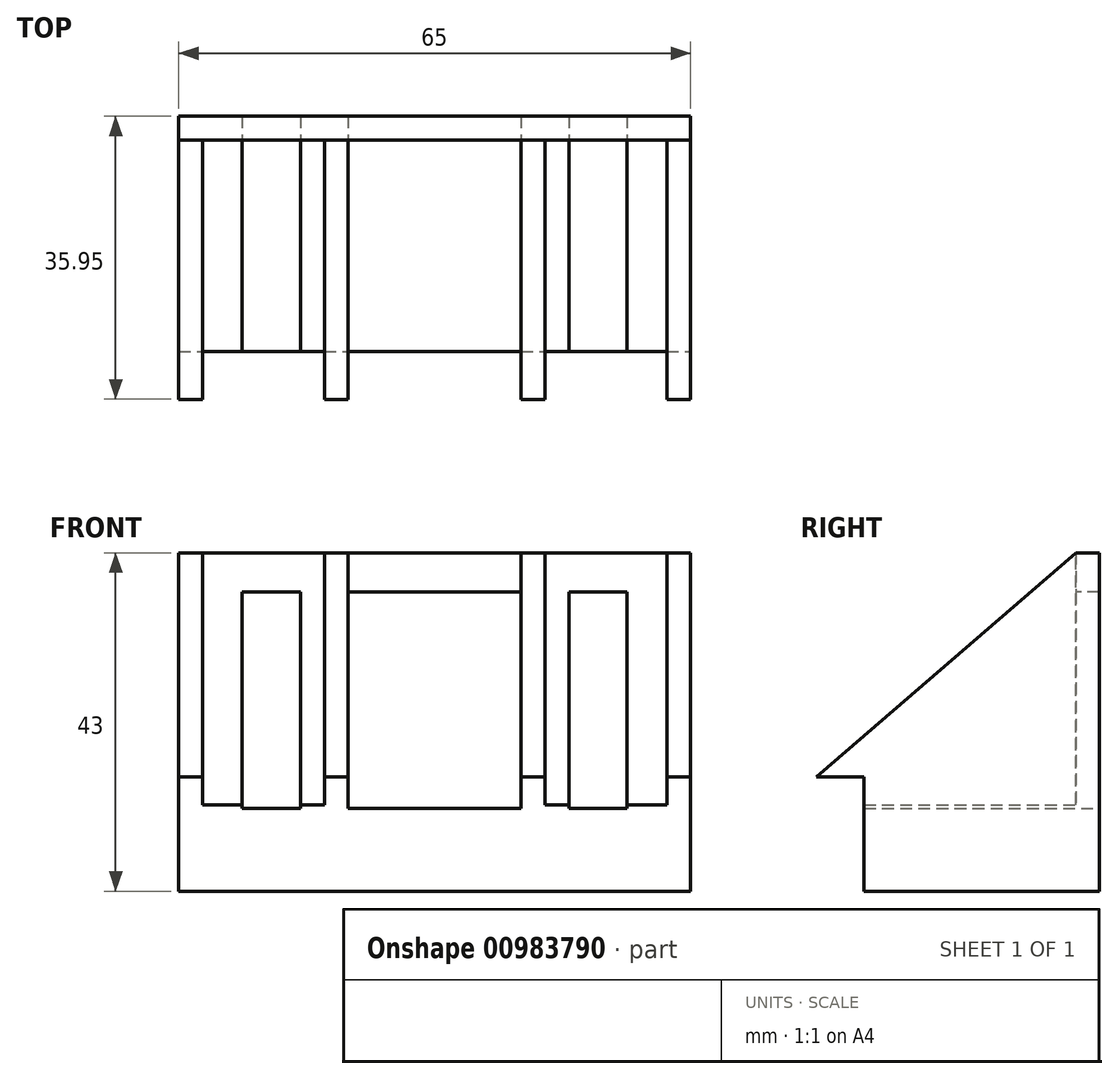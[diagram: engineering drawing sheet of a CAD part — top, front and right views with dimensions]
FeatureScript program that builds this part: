
annotation { "Feature Type Name" : "Feature", "Feature Type Description" : "" }
export const myFeature = defineFeature(function(context is Context, id is Id, definition is map)
    precondition{}
    {
        {
            var Q0;
            Q0=qCreatedBy(makeId("Front.planeOp"),FACE);
            var sketch = newSketch(context, id + "F0", { "sketchPlane" : qUnion([Q0])});
            skLineSegment(sketch, "E0.bottom", {"start": v(-32.5, 17.5) * mm, "end": v(32.5, 17.5) * mm});
            skLineSegment(sketch, "E0.top", {"start": v(-32.5, -17.5) * mm, "end": v(32.5, -17.5) * mm});
            skLineSegment(sketch, "E0.left", {"start": v(-32.5, 17.5) * mm, "end": v(-32.5, -17.5) * mm});
            skLineSegment(sketch, "E0.right", {"start": v(32.5, 17.5) * mm, "end": v(32.5, -17.5) * mm});
            skPoint(sketch, "E0.middle", {"position": v(0, 0) * mm});
            skLineSegment(sketch, "E1.bottom", {"start": v(-20.75, 15) * mm, "end": v(20.75, 15) * mm, "construction": true});
            skLineSegment(sketch, "E1.top", {"start": v(-20.75, -15) * mm, "end": v(20.75, -15) * mm, "construction": true});
            skLineSegment(sketch, "E1.left", {"start": v(-20.75, 15) * mm, "end": v(-20.75, -15) * mm, "construction": true});
            skLineSegment(sketch, "E1.right", {"start": v(20.75, 15) * mm, "end": v(20.75, -15) * mm, "construction": true});
            skLineSegment(sketch, "E2.bottom", {"start": v(-20.75, 15) * mm, "end": v(-24.45, 15) * mm});
            skLineSegment(sketch, "E2.top", {"start": v(-20.75, -15) * mm, "end": v(-24.45, -15) * mm});
            skLineSegment(sketch, "E2.left", {"start": v(-20.75, 15) * mm, "end": v(-20.75, -15) * mm});
            skLineSegment(sketch, "E2.right", {"start": v(-24.45, 15) * mm, "end": v(-24.45, -15) * mm});
            skLineSegment(sketch, "E3.MirrorCS", {"start": v(-17.05, 15) * mm, "end": v(-17.05, -15) * mm});
            skLineSegment(sketch, "E4.MirrorCS", {"start": v(-20.75, 15) * mm, "end": v(-17.05, 15) * mm});
            skLineSegment(sketch, "E5.MirrorCS", {"start": v(-20.75, -15) * mm, "end": v(-17.05, -15) * mm});
            skLineSegment(sketch, "E6.MirrorCS", {"start": v(17.05, 15) * mm, "end": v(17.05, -15) * mm});
            skLineSegment(sketch, "E7.MirrorCS", {"start": v(24.45, 15) * mm, "end": v(24.45, -15) * mm});
            skLineSegment(sketch, "E8.MirrorCS", {"start": v(20.75, -15) * mm, "end": v(24.45, -15) * mm});
            skLineSegment(sketch, "E9.MirrorCS", {"start": v(20.75, -15) * mm, "end": v(-20.75, -15) * mm, "construction": true});
            skLineSegment(sketch, "E10.MirrorCS", {"start": v(20.75, 15) * mm, "end": v(24.45, 15) * mm});
            skLineSegment(sketch, "E11.MirrorCS", {"start": v(20.75, 15) * mm, "end": v(-20.75, 15) * mm, "construction": true});
            skLineSegment(sketch, "E12.bottom", {"start": v(17.05, 15) * mm, "end": v(24.45, 15) * mm});
            skLineSegment(sketch, "E12.top", {"start": v(17.05, -15) * mm, "end": v(24.45, -15) * mm});
            skLineSegment(sketch, "E13.bottom", {"start": v(-11, 15) * mm, "end": v(11, 15) * mm});
            skLineSegment(sketch, "E13.top", {"start": v(-11, -15) * mm, "end": v(11, -15) * mm});
            skLineSegment(sketch, "E13.left", {"start": v(-11, 15) * mm, "end": v(-11, -15) * mm});
            skLineSegment(sketch, "E13.right", {"start": v(11, 15) * mm, "end": v(11, -15) * mm});
            skLineSegment(sketch, "E14.top", {"start": v(-32.5, -14.5) * mm, "end": v(32.5, -14.5) * mm});
            skLineSegment(sketch, "E14.left", {"start": v(-32.5, -17.5) * mm, "end": v(-32.5, -14.5) * mm});
            skLineSegment(sketch, "E14.right", {"start": v(32.5, -17.5) * mm, "end": v(32.5, -14.5) * mm});
            skSolve(sketch);
        }
        {
            var Q0;
            {var subQ15=sQuery(id+"F0.wireOp",EDGE,"E0.bottom");Q0=makeQuery(id+"F0.imprint","IMPRINT",FACE,{"disambiguationData":[TD([[makeQuery(id+"F0.imprint","IMPRINT",EDGE,{"derivedFrom":subQ15}),-1.0]])]});}
            extrude(context, id + "F1", {"entities" : qUnion([Q0]), "depth" : 3 * mm, "offsetDistance" : 25 * mm});
        }
        {
            var Q0;
            {var subQ15=sQuery(id+"F0.wireOp",EDGE,"E0.top");Q0=makeQuery(id+"F0.imprint","IMPRINT",FACE,{"disambiguationData":[TD([[makeQuery(id+"F0.imprint","IMPRINT",EDGE,{"derivedFrom":subQ15}),1.0]])]});}
            extrude(context, id + "F2", {"entities" : qUnion([Q0]), "operationType" : NewBodyOperationType.ADD, "depth" : 40 * mm, "offsetDistance" : 25 * mm});
        }
        {
            var Q0;
            {var subQ0=sQuery(id+"F0.wireOp",EDGE,"E0.left");Q0=makeQuery(id+"F2.boolean.opBoolean","MERGE",FACE,{"derivedFrom":[makeQuery(id+"F1.opExtrude","SWEPT_FACE",FACE,{"disambiguationData":[OSD([subQ0])]}),makeQuery(id+"F2.opExtrude","SWEPT_FACE",FACE,{"disambiguationData":[OSD([subQ0])]})]});}
            var sketch = newSketch(context, id + "F3", { "sketchPlane" : qUnion([Q0])});
            skLineSegment(sketch, "E15", {"start": v(3, 17.5) * mm, "end": v(40, -14.5) * mm});
            skLineSegment(sketch, "E16", {"start": v(40, -14.5) * mm, "end": v(3, -14.5) * mm});
            skLineSegment(sketch, "E17", {"start": v(3, -14.5) * mm, "end": v(3, 17.5) * mm});
            skLineSegment(sketch, "E18", {"start": v(3, 17.5) * mm, "end": v(45.34, 20.76) * mm});
            skLineSegment(sketch, "E19", {"start": v(45.34, 20.76) * mm, "end": v(40, -14.5) * mm});
            skSolve(sketch);
        }
        {
            var Q0;
            Q0=makeQuery(id+"F1.opExtrude","CAP_FACE",FACE,{"disambiguationData":[OSD([sQuery(id+"F0.wireOp",EDGE,"E0.bottom"),sQuery(id+"F0.wireOp",EDGE,"E0.left"),sQuery(id+"F0.wireOp",EDGE,"E0.right"),sQuery(id+"F0.wireOp",EDGE,"E2.bottom"),sQuery(id+"F0.wireOp",EDGE,"E2.right"),sQuery(id+"F0.wireOp",EDGE,"E3.MirrorCS"),sQuery(id+"F0.wireOp",EDGE,"E4.MirrorCS"),sQuery(id+"F0.wireOp",EDGE,"E6.MirrorCS"),sQuery(id+"F0.wireOp",EDGE,"E7.MirrorCS"),sQuery(id+"F0.wireOp",EDGE,"E10.MirrorCS"),sQuery(id+"F0.wireOp",EDGE,"E12.bottom"),sQuery(id+"F0.wireOp",EDGE,"E13.bottom"),sQuery(id+"F0.wireOp",EDGE,"E13.left"),sQuery(id+"F0.wireOp",EDGE,"E13.right"),sQuery(id+"F0.wireOp",EDGE,"E14.top")])],"isStart":false});
            var sketch = newSketch(context, id + "F4", { "sketchPlane" : qUnion([Q0])});
            skLineSegment(sketch, "E20.bottom", {"start": v(-11, -14.5) * mm, "end": v(-14, -14.5) * mm});
            skLineSegment(sketch, "E20.top", {"start": v(-11, 17.5) * mm, "end": v(-14, 17.5) * mm});
            skLineSegment(sketch, "E20.left", {"start": v(-11, -14.5) * mm, "end": v(-11, 17.5) * mm});
            skLineSegment(sketch, "E20.right", {"start": v(-14, -14.5) * mm, "end": v(-14, 17.5) * mm});
            skLineSegment(sketch, "E21.MirrorCS", {"start": v(11, -14.5) * mm, "end": v(11, 17.5) * mm});
            skLineSegment(sketch, "E22.MirrorCS", {"start": v(14, -14.5) * mm, "end": v(14, 17.5) * mm});
            skLineSegment(sketch, "E23.MirrorCS", {"start": v(11, -14.5) * mm, "end": v(14, -14.5) * mm});
            skLineSegment(sketch, "E24.MirrorCS", {"start": v(11, 17.5) * mm, "end": v(14, 17.5) * mm});
            skSolve(sketch);
        }
        {
            var Q0;
            {var subQ3=sQuery(id+"F4.wireOp",EDGE,"E20.bottom");Q0=makeQuery(id+"F4.imprint","IMPRINT",FACE,{"disambiguationData":[TD([[makeQuery(id+"F4.imprint","IMPRINT",EDGE,{"derivedFrom":subQ3}),1.0]])]});}
            var Q1;
            Q1=makeQuery(id+"F4.imprint","IMPRINT",FACE,{"disambiguationData":[TD([[makeQuery(id+"F4.imprint","IMPRINT",EDGE,{"derivedFrom":sQuery(id+"F4.wireOp",EDGE,"E22.MirrorCS")}),1.0]])]});
            extrude(context, id + "F5", {"entities" : qUnion([Q0, Q1]), "operationType" : NewBodyOperationType.ADD, "depth" : 37 * mm, "offsetDistance" : 25 * mm});
        }
        {
            var Q0;
            {var subQ0=sQuery(id+"F0.wireOp",EDGE,"E0.right");Q0=makeQuery(id+"F2.boolean.opBoolean","MERGE",FACE,{"derivedFrom":[makeQuery(id+"F1.opExtrude","SWEPT_FACE",FACE,{"disambiguationData":[OSD([subQ0])]}),makeQuery(id+"F2.opExtrude","SWEPT_FACE",FACE,{"disambiguationData":[OSD([subQ0])]})]});}
            var sketch = newSketch(context, id + "F6", { "sketchPlane" : qUnion([Q0])});
            skLineSegment(sketch, "E25", {"start": v(-3, 17.5) * mm, "end": v(-40, -14.5) * mm});
            skLineSegment(sketch, "E26", {"start": v(-40, -14.5) * mm, "end": v(-3, -14.5) * mm});
            skLineSegment(sketch, "E27", {"start": v(-3, -14.5) * mm, "end": v(-3, 17.5) * mm});
            skSolve(sketch);
        }
        {
            var Q0;
            Q0=makeQuery(id+"F6.imprint","IMPRINT",FACE,{"disambiguationData":[TD([[makeQuery(id+"F6.imprint","IMPRINT",EDGE,{"derivedFrom":sQuery(id+"F6.wireOp",EDGE,"E25")}),1.0]])]});
            extrude(context, id + "F7", {"entities" : qUnion([Q0]), "operationType" : NewBodyOperationType.ADD, "depth" : -3 * mm, "offsetDistance" : 25 * mm});
        }
        {
            var Q0;
            Q0=makeQuery(id+"F3.imprint","IMPRINT",FACE,{"disambiguationData":[TD([[makeQuery(id+"F3.imprint","IMPRINT",EDGE,{"derivedFrom":sQuery(id+"F3.wireOp",EDGE,"E15")}),-1.0]])]});
            extrude(context, id + "F8", {"entities" : qUnion([Q0]), "operationType" : NewBodyOperationType.ADD, "depth" : -3 * mm, "offsetDistance" : 25 * mm});
        }
        {
            var Q0;
            Q0=makeQuery(id+"F3.imprint","IMPRINT",FACE,{"disambiguationData":[TD([[makeQuery(id+"F3.imprint","IMPRINT",EDGE,{"derivedFrom":sQuery(id+"F3.wireOp",EDGE,"E15")}),1.0]])]});
            extrude(context, id + "F9", {"entities" : qUnion([Q0]), "operationType" : NewBodyOperationType.REMOVE, "oppositeDirection" : true, "depth" : 90 * mm, "offsetDistance" : 25 * mm});
        }
        {
            var Q0;
            Q0=makeQuery(id+"F2.opExtrude","SWEPT_FACE",FACE,{"disambiguationData":[OSD([sQuery(id+"F0.wireOp",EDGE,"E0.top")])]});
            extrude(context, id + "F10", {"entities" : qUnion([Q0]), "operationType" : NewBodyOperationType.ADD, "depth" : 8 * mm, "offsetDistance" : 25 * mm});
        }
        {
            var Q0;
            Q0=makeQuery(id+"F10.opExtrude","CAP_FACE",FACE,{"disambiguationData":[OSD([sQuery(id+"F0.wireOp",EDGE,"E0.top")])],"isStart":false});
            var sketch = newSketch(context, id + "F11", { "sketchPlane" : qUnion([Q0])});
            skLineSegment(sketch, "E28", {"start": v(-29.5, -16.45) * mm, "end": v(-14, -16.45) * mm, "construction": true});
            skCircle(sketch, "E29", {"center": v(-21.75, -16.45) * mm, "radius": 4 * mm});
            skCircle(sketch, "E30", {"center": v(-21.75, -16.45) * mm, "radius": 1.4 * mm});
            skCircle(sketch, "E31.MirrorC", {"center": v(21.75, -16.45) * mm, "radius": 4 * mm});
            skCircle(sketch, "E32.MirrorC", {"center": v(21.75, -16.45) * mm, "radius": 1.4 * mm});
            skSolve(sketch);
        }
        {
            var Q0;
            Q0=makeQuery(id+"F11.imprint","IMPRINT",FACE,{"disambiguationData":[TD([[makeQuery(id+"F11.imprint","IMPRINT",EDGE,{"derivedFrom":sQuery(id+"F11.wireOp",EDGE,"E29")}),1.0]])]});
            var Q1;
            Q1=makeQuery(id+"F11.imprint","IMPRINT",FACE,{"disambiguationData":[TD([[makeQuery(id+"F11.imprint","IMPRINT",EDGE,{"derivedFrom":sQuery(id+"F11.wireOp",EDGE,"E31.MirrorC")}),-1.0]])]});
            extrude(context, id + "F12", {"entities" : qUnion([Q0, Q1]), "operationType" : NewBodyOperationType.REMOVE, "oppositeDirection" : true, "depth" : 15 * mm, "offsetDistance" : 25 * mm});
        }
        {
            var Q0;
            Q0=makeQuery(id+"F11.imprint","IMPRINT",FACE,{"disambiguationData":[TD([[makeQuery(id+"F11.imprint","IMPRINT",EDGE,{"derivedFrom":sQuery(id+"F11.wireOp",EDGE,"E30")}),1.0]])]});
            var Q1;
            Q1=makeQuery(id+"F11.imprint","IMPRINT",FACE,{"disambiguationData":[TD([[makeQuery(id+"F11.imprint","IMPRINT",EDGE,{"derivedFrom":sQuery(id+"F11.wireOp",EDGE,"E32.MirrorC")}),-1.0]])]});
            extrude(context, id + "F13", {"entities" : qUnion([Q0, Q1]), "operationType" : NewBodyOperationType.REMOVE, "oppositeDirection" : true, "depth" : 18 * mm, "offsetDistance" : 25 * mm});
        }
        {
            var Q0;
            {var subQ0=sQuery(id+"F0.wireOp",EDGE,"E0.right");Q0=makeQuery(id+"F10.boolean.opBoolean","MERGE",FACE,{"derivedFrom":[makeQuery(id+"F7.boolean.opBoolean","MERGE",FACE,{"derivedFrom":[makeQuery(id+"F2.boolean.opBoolean","MERGE",FACE,{"derivedFrom":[makeQuery(id+"F1.opExtrude","SWEPT_FACE",FACE,{"disambiguationData":[OSD([subQ0])]}),makeQuery(id+"F2.opExtrude","SWEPT_FACE",FACE,{"disambiguationData":[OSD([subQ0])]})]}),makeQuery(id+"F7.opExtrude","CAP_FACE",FACE,{"disambiguationData":[OSD([sQuery(id+"F6.wireOp",EDGE,"E25"),sQuery(id+"F6.wireOp",EDGE,"E26"),sQuery(id+"F6.wireOp",EDGE,"E27")])],"isStart":true})]}),makeQuery(id+"F10.opExtrude","SWEPT_FACE",FACE,{"disambiguationData":[OSD([sQuery(id+"F0.wireOp",EDGE,"E0.top"),subQ0])]})]});}
            var sketch = newSketch(context, id + "F14", { "sketchPlane" : qUnion([Q0])});
            skLineSegment(sketch, "E33.bottom", {"start": v(-29.9, -11) * mm, "end": v(-40, -11) * mm});
            skLineSegment(sketch, "E33.top", {"start": v(-29.9, -29) * mm, "end": v(-40, -29) * mm});
            skLineSegment(sketch, "E33.left", {"start": v(-29.9, -11) * mm, "end": v(-29.9, -29) * mm});
            skLineSegment(sketch, "E33.right", {"start": v(-40, -11) * mm, "end": v(-40, -29) * mm});
            skSolve(sketch);
        }
        {
            var Q0;
            Q0 = qSketchRegion(id + "F14", true);
            extrude(context, id + "F15", {"entities" : qUnion([Q0]), "operationType" : NewBodyOperationType.REMOVE, "oppositeDirection" : true, "depth" : 101.4 * mm, "offsetDistance" : 25 * mm});
        }
        {
            var Q0;
            Q0=makeQuery(id+"F5.boolean.opBoolean","MERGE",FACE,{"derivedFrom":[makeQuery(id+"F1.opExtrude","SWEPT_FACE",FACE,{"disambiguationData":[OSD([sQuery(id+"F0.wireOp",EDGE,"E0.bottom")])]}),makeQuery(id+"F5.opExtrude","SWEPT_FACE",FACE,{"disambiguationData":[OSD([sQuery(id+"F4.wireOp",EDGE,"E20.top")])]}),makeQuery(id+"F5.opExtrude","SWEPT_FACE",FACE,{"disambiguationData":[OSD([sQuery(id+"F4.wireOp",EDGE,"E24.MirrorCS")])]})]});
            extrude(context, id + "F16", {"entities" : qUnion([Q0]), "operationType" : NewBodyOperationType.ADD, "depth" : -5 * mm, "offsetDistance" : 25 * mm});
        }
    });
